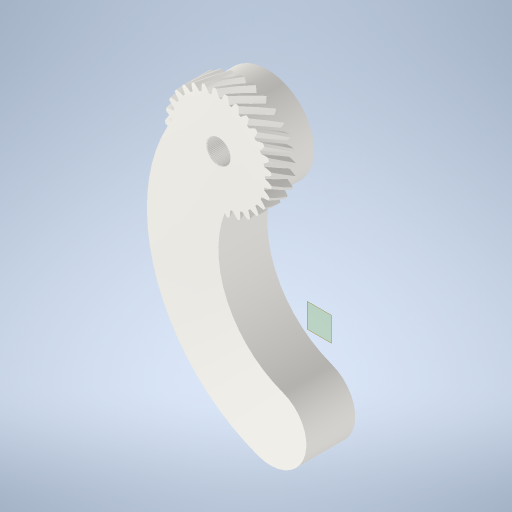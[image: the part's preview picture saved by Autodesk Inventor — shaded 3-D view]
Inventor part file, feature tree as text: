
AUTODESK INVENTOR PART (.ipt)
format: ipt  version: 2024 (Build 280153000, 153)  size: 1,927,168 bytes
history: native  units: mm (DEFAULTED — no unit token found)
features: reference x193, other x8, extrude x4, plane x4, sketch x4, projected_geometry x1
ambient origin geometry x8: Origin, YZ Plane, XZ Plane, XY Plane, X Axis, Y Axis, Z Axis, Center Point
bodies: Solid1 (feature_tree)
feature tree (214):
  extrude  "Extrusion1"  Depth=5.0mm TaperAngle=0.0deg
  plane  "Work Plane2"
  plane  "Work Plane8"
  plane  "Work Plane9"
  other  "Spur Gear"
  extrude  "Extrusion2"  Depth=10.0mm TaperAngle=0.0deg
  plane  "Work Plane11"
  extrude  "Extrusion3"  Depth=20.0mm TaperAngle=0.0deg
  extrude  "Extrusion4"  TaperAngle=0.0deg  [1 undecoded]
  sketch  "Sketch1"  dims[d0=21.801031mm d1=5.0mm d2=0.0mm]
  other  "Srf1"
  sketch  "Sketch3"  dims[d3=20.091789mm d4=10.0mm d5=0.0mm]
  sketch  "Sketch4"  dims[d16=20.0mm d17=0.0mm d34=1.083308mm]
  reference  "Reference1"
  reference  "Reference2"
  reference  "Reference3"
  reference  "Reference4"
  reference  "Reference5"
  reference  "Reference6"
  reference  "Reference7"
  reference  "Reference8"
  reference  "Reference9"
  reference  "Reference10"
  reference  "Reference11"
  reference  "Reference12"
  reference  "Reference13"
  reference  "Reference14"
  reference  "Reference15"
  reference  "Reference16"
  reference  "Reference17"
  reference  "Reference18"
  reference  "Reference19"
  reference  "Reference20"
  reference  "Reference21"
  reference  "Reference22"
  reference  "Reference23"
  reference  "Reference24"
  reference  "Reference25"
  reference  "Reference26"
  reference  "Reference27"
  reference  "Reference28"
  reference  "Reference29"
  reference  "Reference30"
  reference  "Reference31"
  reference  "Reference32"
  reference  "Reference33"
  reference  "Reference34"
  reference  "Reference35"
  reference  "Reference36"
  reference  "Reference37"
  reference  "Reference38"
  reference  "Reference39"
  reference  "Reference40"
  reference  "Reference41"
  reference  "Reference42"
  reference  "Reference43"
  reference  "Reference44"
  reference  "Reference45"
  reference  "Reference46"
  reference  "Reference47"
  reference  "Reference48"
  reference  "Reference49"
  reference  "Reference50"
  reference  "Reference51"
  reference  "Reference52"
  reference  "Reference53"
  reference  "Reference54"
  reference  "Reference55"
  reference  "Reference56"
  reference  "Reference57"
  reference  "Reference58"
  reference  "Reference59"
  reference  "Reference60"
  reference  "Reference61"
  reference  "Reference62"
  reference  "Reference63"
  reference  "Reference64"
  reference  "Reference65"
  reference  "Reference66"
  reference  "Reference67"
  reference  "Reference68"
  reference  "Reference69"
  reference  "Reference70"
  reference  "Reference71"
  reference  "Reference72"
  reference  "Reference73"
  reference  "Reference74"
  reference  "Reference75"
  reference  "Reference76"
  reference  "Reference77"
  reference  "Reference78"
  reference  "Reference79"
  reference  "Reference80"
  reference  "Reference81"
  reference  "Reference82"
  reference  "Reference83"
  reference  "Reference84"
  reference  "Reference85"
  reference  "Reference86"
  reference  "Reference87"
  reference  "Reference88"
  reference  "Reference89"
  reference  "Reference90"
  reference  "Reference91"
  reference  "Reference92"
  reference  "Reference93"
  reference  "Reference94"
  reference  "Reference95"
  reference  "Reference96"
  reference  "Reference97"
  reference  "Reference98"
  reference  "Reference99"
  reference  "Reference100"
  reference  "Reference101"
  reference  "Reference102"
  reference  "Reference103"
  reference  "Reference104"
  reference  "Reference105"
  reference  "Reference106"
  reference  "Reference107"
  reference  "Reference108"
  reference  "Reference109"
  reference  "Reference110"
  reference  "Reference111"
  reference  "Reference112"
  reference  "Reference113"
  reference  "Reference114"
  reference  "Reference115"
  reference  "Reference116"
  reference  "Reference117"
  reference  "Reference118"
  reference  "Reference119"
  reference  "Reference120"
  reference  "Reference121"
  reference  "Reference122"
  reference  "Reference123"
  reference  "Reference124"
  reference  "Reference125"
  reference  "Reference126"
  reference  "Reference127"
  reference  "Reference128"
  reference  "Reference129"
  reference  "Reference130"
  reference  "Reference131"
  reference  "Reference132"
  reference  "Reference133"
  reference  "Reference134"
  reference  "Reference135"
  reference  "Reference136"
  reference  "Reference137"
  reference  "Reference138"
  reference  "Reference139"
  reference  "Reference140"
  reference  "Reference141"
  reference  "Reference142"
  reference  "Reference143"
  reference  "Reference144"
  reference  "Reference145"
  reference  "Reference146"
  reference  "Reference147"
  reference  "Reference148"
  reference  "Reference149"
  reference  "Reference150"
  reference  "Reference151"
  reference  "Reference152"
  reference  "Reference153"
  reference  "Reference154"
  reference  "Reference155"
  reference  "Reference156"
  reference  "Reference157"
  reference  "Reference158"
  reference  "Reference159"
  reference  "Reference160"
  reference  "Reference161"
  reference  "Reference162"
  reference  "Reference163"
  reference  "Reference164"
  reference  "Reference165"
  reference  "Reference166"
  reference  "Reference167"
  reference  "Reference168"
  reference  "Reference169"
  reference  "Reference170"
  reference  "Reference171"
  reference  "Reference172"
  reference  "Reference173"
  reference  "Reference174"
  reference  "Reference175"
  reference  "Reference176"
  reference  "Reference177"
  reference  "Reference178"
  reference  "Reference179"
  reference  "Reference180"
  reference  "Reference181"
  reference  "Reference182"
  reference  "Reference183"
  reference  "Reference184"
  reference  "Reference185"
  reference  "Reference186"
  reference  "Reference187"
  reference  "Reference188"
  reference  "Reference189"
  reference  "Reference190"
  reference  "Reference191"
  reference  "Reference192"
  reference  "Reference193"
  sketch  "Sketch5"  dims[d39=0.0mm d41=0.0mm d43=20.0mm d46=20.0mm d47=0.0mm d48=0.0mm d49=5.0mm d50=10.0mm d51=0.0mm d52=2.0mm d53=3.0mm d54=0.0mm d55=0.0mm d56=40.0mm d57=10.0mm d58=10.0mm d59=20.0mm d62=10.0mm d63=0.0mm d64=43.0mm d65=19.112054mm]
  projected_geometry  "Projected Loop1"
  other  "Pitch Diameter"
  other  "<userpath> windows\Documents\Inventor\Robotska_roka\Assembly4.iam"
  other  "Assembly4.iam"
  other  "SG90 - Micro Servo 9g - Tower Pro:3"
  other  "Tower Pro - Micro Servo 9g - SG90.1_12"
  other  "Tower Pro - Micro Servo 9g - SG90.1_11"
note: 1 required parameter value undecoded (feature->parameter linkage not recoverable at this tier; creation-order binding heuristic only, values carry confidence <= 0.55)
